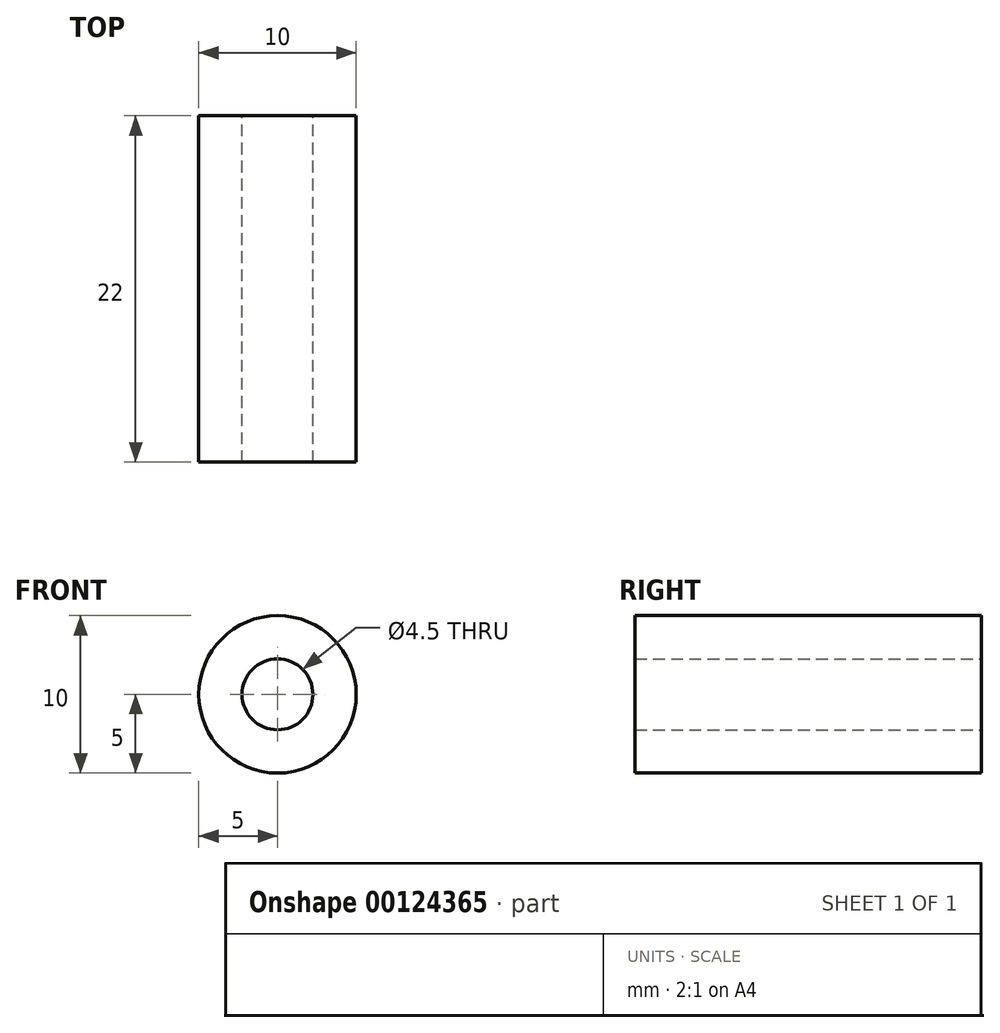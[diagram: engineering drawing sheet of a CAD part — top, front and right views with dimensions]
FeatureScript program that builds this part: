
annotation { "Feature Type Name" : "Feature", "Feature Type Description" : "" }
export const myFeature = defineFeature(function(context is Context, id is Id, definition is map)
    precondition{}
    {
        {
            var Q0;
            Q0=qCreatedBy(makeId("Front.planeOp"),FACE);
            var sketch = newSketch(context, id + "F0", { "sketchPlane" : qUnion([Q0])});
            skCircle(sketch, "E0", {"center": v(0, 0) * mm, "radius": 2.25 * mm});
            skCircle(sketch, "E1", {"center": v(0, 0) * mm, "radius": 5 * mm});
            skSolve(sketch);
        }
        {
            var Q0;
            Q0=makeQuery(id+"F0.imprint","IMPRINT",FACE,{"disambiguationData":[TD([[makeQuery(id+"F0.imprint","IMPRINT",EDGE,{"derivedFrom":sQuery(id+"F0.wireOp",EDGE,"E0")}),-1.0]])]});
            extrude(context, id + "F1", {"entities" : qUnion([Q0]), "depth" : 22 * mm});
        }
    });
